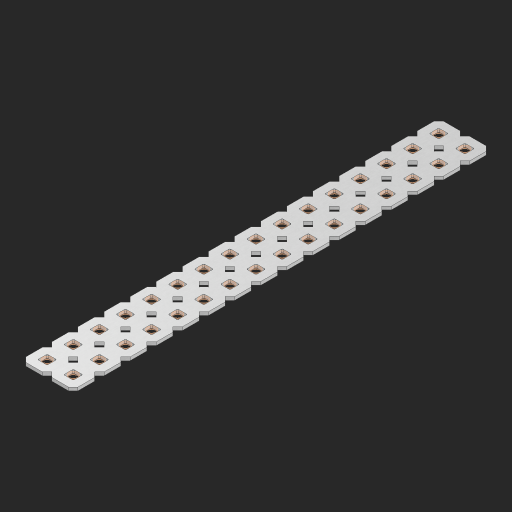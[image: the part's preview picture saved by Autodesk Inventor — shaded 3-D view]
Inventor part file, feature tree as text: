
AUTODESK INVENTOR PART (.ipt)
format: ipt  version: 2023 (Build 270158000, 158)  size: 638,464 bytes
history: native  units: in
note: dims shown in document units (in); Inventor stores cm internally (conversion verified against a paired STEP export)
features: other x33, extrude x31, sketch x2, pattern_linear x1
ambient origin geometry x8: Origin, YZ Plane, XZ Plane, XY Plane, X Axis, Y Axis, Z Axis, Center Point
bodies: Solid1 (feature_tree), Body (feature_tree)
feature tree (67):
  pattern_linear  "Rectangular Pattern1"  Spacing1=0.09in  [1 undecoded]
  sketch  "Sketch1"  dims[d1=0.5in]
  sketch  "Sketch2"  dims[d2=0.182in d3=0.09in d4=0.09in d5=0.09in d6=0.09in d7=0.09in d8=0.09in d9=0.09in d10=0.09in d11=0.02in d13=0.0in d14=0.172in d15=0.0625in d16=0.0in d19=0.5in d22=0.5in]
  other  "Srf1"
  other  "Srf126"
  other  "Srf127"
  other  "Srf128"
  other  "Srf129"
  other  "Srf130"
  other  "Srf131"
  other  "Srf250"
  other  "Srf251"
  other  "Srf252"
  other  "Srf253"
  other  "Srf254"
  other  "Srf255"
  other  "Srf256"
  other  "Srf257"
  other  "Srf258"
  other  "Srf268"
  other  "Srf269"
  other  "Srf270"
  other  "Srf271"
  other  "Srf272"
  other  "Srf273"
  other  "Srf274"
  other  "Srf275"
  other  "Srf276"
  other  "Srf277"
  other  "Srf278"
  other  "Srf279"
  other  "Srf280"
  other  "Srf281"
  other  "Srf282"
  other  "Srf283"
  other  "Circle"
  extrude  "ExtrusionSrf126"  Depth=0.09in
  extrude  "ExtrusionSrf127"  Depth=0.09in
  extrude  "ExtrusionSrf128"  Depth=0.09in
  extrude  "ExtrusionSrf129"  Depth=0.09in
  extrude  "ExtrusionSrf130"  Depth=0.09in
  extrude  "ExtrusionSrf131"  Depth=0.09in
  extrude  "ExtrusionSrf250"  Depth=0.09in
  extrude  "ExtrusionSrf251"  Depth=0.02in
  extrude  "ExtrusionSrf252"  TaperAngle=0.0deg  [1 undecoded]
  extrude  "ExtrusionSrf253"  Depth=0.5in
  extrude  "ExtrusionSrf254"  Depth=0.0625in TaperAngle=0.0deg
  extrude  "ExtrusionSrf255"  Depth=0.5in
  extrude  "ExtrusionSrf256"  Depth=0.5in
  extrude  "ExtrusionSrf257"  [1 undecoded]
  extrude  "ExtrusionSrf258"  [1 undecoded]
  extrude  "ExtrusionSrf268"  [1 undecoded]
  extrude  "ExtrusionSrf269"  [1 undecoded]
  extrude  "ExtrusionSrf270"  [1 undecoded]
  extrude  "ExtrusionSrf271"  [1 undecoded]
  extrude  "ExtrusionSrf272"  [1 undecoded]
  extrude  "ExtrusionSrf273"  [1 undecoded]
  extrude  "ExtrusionSrf274"  [1 undecoded]
  extrude  "ExtrusionSrf275"  [1 undecoded]
  extrude  "ExtrusionSrf276"  [1 undecoded]
  extrude  "ExtrusionSrf277"  [1 undecoded]
  extrude  "ExtrusionSrf278"  [1 undecoded]
  extrude  "ExtrusionSrf279"  [1 undecoded]
  extrude  "ExtrusionSrf280"  [1 undecoded]
  extrude  "ExtrusionSrf281"  [1 undecoded]
  extrude  "ExtrusionSrf282"  [1 undecoded]
  extrude  "ExtrusionSrf283"  [1 undecoded]
note: 20 required parameter values undecoded (feature->parameter linkage not recoverable at this tier; creation-order binding heuristic only, values carry confidence <= 0.55)
